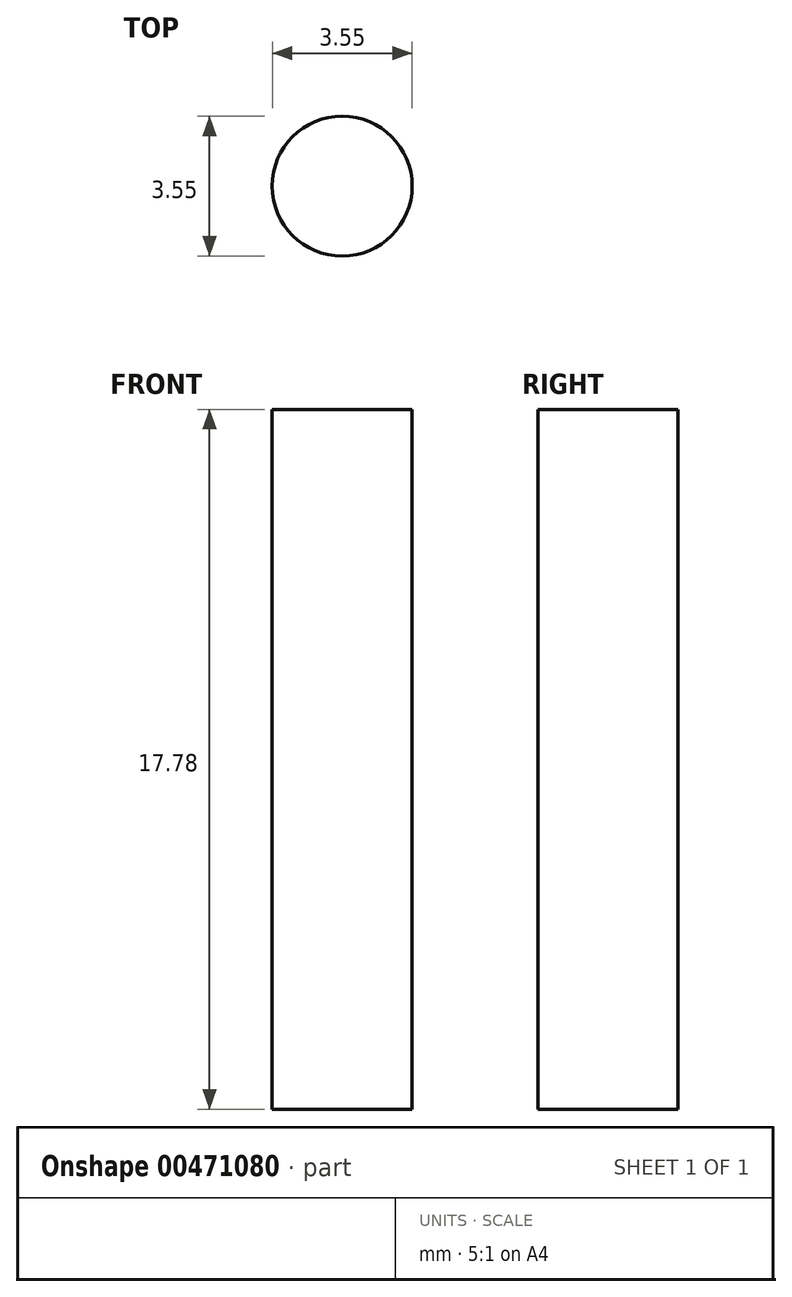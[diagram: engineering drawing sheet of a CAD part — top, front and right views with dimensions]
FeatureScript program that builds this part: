
annotation { "Feature Type Name" : "Feature", "Feature Type Description" : "" }
export const myFeature = defineFeature(function(context is Context, id is Id, definition is map)
    precondition{}
    {
        {
            var Q0;
            Q0=qCreatedBy(makeId("Top.planeOp"),FACE);
            var sketch = newSketch(context, id + "F0", { "sketchPlane" : qUnion([Q0])});
            skCircle(sketch, "E0", {"center": v(-7.08, 7.9) * mm, "radius": 1.78 * mm});
            skSolve(sketch);
        }
        {
            var Q0;
            Q0=makeQuery(id+"F0.imprint","IMPRINT",FACE,{"disambiguationData":[TD([[makeQuery(id+"F0.imprint","IMPRINT",EDGE,{"derivedFrom":sQuery(id+"F0.wireOp",EDGE,"E0")}),1.0]])]});
            extrude(context, id + "F1", {"entities" : qUnion([Q0]), "depth" : 17.78 * mm, "offsetDistance" : 25.4 * mm});
        }
    });
